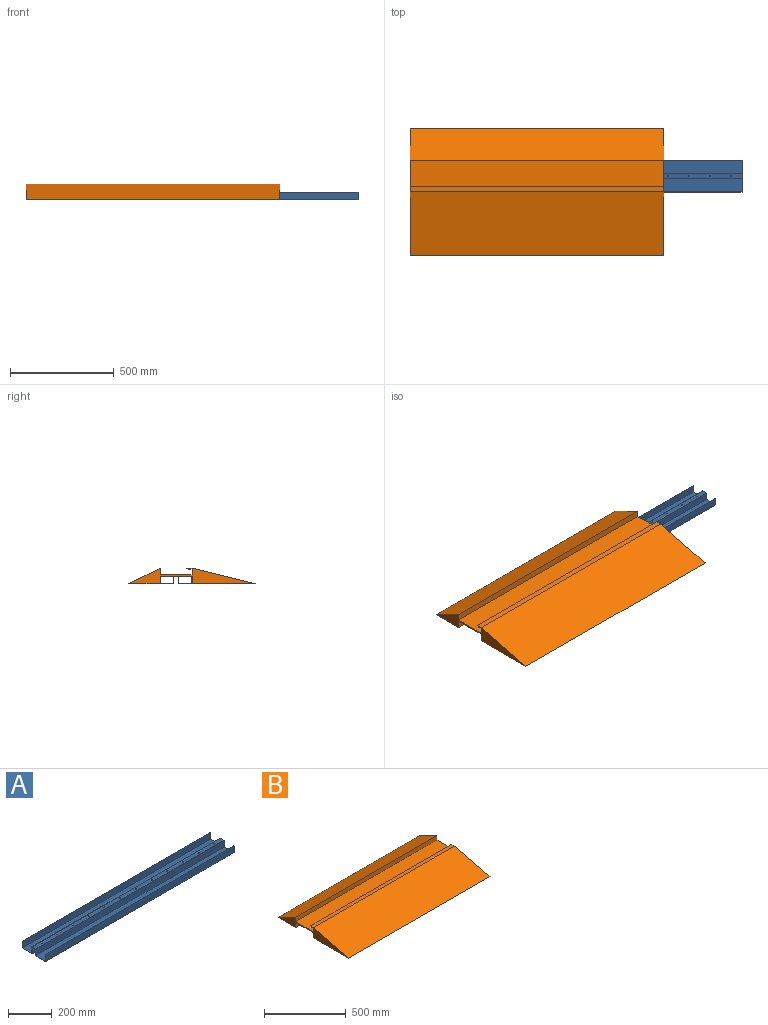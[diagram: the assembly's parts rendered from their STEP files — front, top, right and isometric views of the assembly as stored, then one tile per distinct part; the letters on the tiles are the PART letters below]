
ASSEMBLY  parts=2 mates=2
PART A: 30 faces, bbox 1219.2x152.4x38.1 mm
  f0: cylinder r=2.38mm len=4.76mm, axis (0,0,1), area 19mm2, adj f15,f23
  f1: cylinder r=2.38mm len=4.76mm, axis (0,0,1), area 19mm2, adj f15,f23
  f2: cylinder r=2.38mm len=4.76mm, axis (0,0,1), area 19mm2, adj f15,f23
  f3: cylinder r=2.38mm len=4.76mm, axis (0,0,1), area 19mm2, adj f15,f23
  f4: cylinder r=2.38mm len=4.76mm, axis (0,0,1), area 19mm2, adj f15,f23
  f5: cylinder r=2.38mm len=4.76mm, axis (0,0,1), area 19mm2, adj f15,f23
  f6: cylinder r=2.38mm len=4.76mm, axis (0,0,1), area 19mm2, adj f15,f23
  f7: cylinder r=2.38mm len=4.76mm, axis (0,0,1), area 19mm2, adj f15,f23
  f8: cylinder r=2.38mm len=4.76mm, axis (0,0,1), area 19mm2, adj f15,f23
  f9: cylinder r=2.38mm len=4.76mm, axis (0,0,1), area 19mm2, adj f15,f23
  f10: cylinder r=2.38mm len=4.76mm, axis (0,0,1), area 19mm2, adj f15,f23
  f11: plane 1219.2x1.27mm, normal (0,0,1), area 1548.4mm2, adj f12,f26,f27,f28
  f12: plane 1219.2x38.1mm, normal (0,-1,0), area 46451.5mm2, adj f11,f13,f27,f28
  f13: plane 1219.2x64.77mm, normal (0,0,-1), area 78967.6mm2, adj f12,f14,f27,f28
  f14: plane 1219.2x36.83mm, normal (0,1,0), area 44903.1mm2, adj f13,f15,f27,f28
  f15: plane 1219.2x22.86mm, normal (0,0,-1), area 27657.1mm2, adj f0,f1,f2,f3,f4,f5,f6,f7
  f16: plane 1219.2x36.83mm, normal (0,-1,0), area 44903.1mm2, adj f15,f17,f27,f28
  f17: plane 1219.2x64.77mm, normal (0,0,-1), area 78967.6mm2, adj f16,f18,f27,f28
  f18: plane 1219.2x38.1mm, normal (0,1,0), area 46451.5mm2, adj f17,f19,f27,f28
  f19: plane 1219.2x1.27mm, normal (0,0,1), area 1548.4mm2, adj f18,f20,f27,f28
  f20: plane 1219.2x36.83mm, normal (0,-1,0), area 44903.1mm2, adj f19,f21,f27,f28
  f21: plane 1219.2x62.23mm, normal (0,0,1), area 75870.8mm2, adj f20,f22,f27,f28
  f22: plane 1219.2x36.83mm, normal (0,1,0), area 44903.1mm2, adj f21,f23,f27,f28
  f23: plane 1219.2x25.4mm, normal (0,0,1), area 30753.9mm2, adj f0,f1,f2,f3,f4,f5,f6,f7
  f24: plane 1219.2x36.83mm, normal (0,-1,0), area 44903.1mm2, adj f23,f25,f27,f28
  f25: plane 1219.2x62.23mm, normal (0,0,1), area 75870.8mm2, adj f24,f26,f27,f28
  f26: plane 1219.2x36.83mm, normal (0,1,0), area 44903.1mm2, adj f11,f25,f27,f28
  f27: plane 152.4x38.1mm, normal (1,0,0), area 380.6mm2, adj f11,f12,f13,f14,f15,f16,f17,f18
  f28: plane 152.4x38.1mm, normal (-1,0,0), area 380.6mm2, adj f11,f12,f13,f14,f15,f16,f17,f18
  f29: cylinder r=2.38mm len=4.76mm, axis (0,0,1), area 19mm2, adj f15,f23
PART B: 15 faces, bbox 1219.2x609.6x76.2 mm
  f0: plane 1219.2x38.1mm, normal (0,1,0), area 46451.5mm2, adj f1,f12,f13,f14
  f1: plane 1219.2x152.4mm, normal (0,0,-1), area 185806.1mm2, adj f0,f2,f13,f14
  f2: plane 1219.2x38.1mm, normal (0,-1,0), area 46451.5mm2, adj f1,f3,f13,f14
  f3: plane 1219.2x152.4mm, normal (0,0,-1), area 185806.1mm2, adj f2,f4,f13,f14
  f4: plane 1219.2x152.4mm, normal (0,0.45,0.89), area 207737.5mm2, adj f3,f5,f13,f14
  f5: plane 1219.2x31.75mm, normal (0,-1,0), area 38709.6mm2, adj f4,f6,f13,f14
  f6: plane 1219.2x152.4mm, normal (0,0,1), area 185806.1mm2, adj f5,f7,f13,f14
  f7: plane 1219.2x25.4mm, normal (0,1,0), area 30967.7mm2, adj f6,f8,f13,f14
  f8: plane 1219.2x19.05mm, normal (0,0,-1), area 23225.8mm2, adj f7,f9,f13,f14
  f9: plane 1219.2x6.35mm, normal (0,0.71,-0.71), area 10948.7mm2, adj f8,f10,f13,f14
  f10: plane 1219.2x25.4mm, normal (0,0,1), area 30967.7mm2, adj f9,f11,f13,f14
  f11: plane 1219.2x304.8mm, normal (0,-0.24,0.97), area 383049mm2, adj f10,f12,f13,f14
  f12: plane 1219.2x304.8mm, normal (0,0,-1), area 371612.2mm2, adj f0,f11,f13,f14
  f13: plane 609.6x76.2mm, normal (1,0,0), area 18528.2mm2, adj f0,f1,f2,f3,f4,f5,f6,f7
  f14: plane 609.6x76.2mm, normal (-1,0,0), area 18528.2mm2, adj f0,f1,f2,f3,f4,f5,f6,f7
PLACE A t=(191.96,7.33,-145.55)mm
PLACE B t=(-794.91,-68.87,-164.6)mm fixed
MATE planar A.f12 <-> B.f0  axis (0,-1,0) through (191.96,-68.87,-145.55)mm
MATE planar A.f23 <-> B.f1  axis (0,0,1) through (191.96,7.33,-126.5)mm
